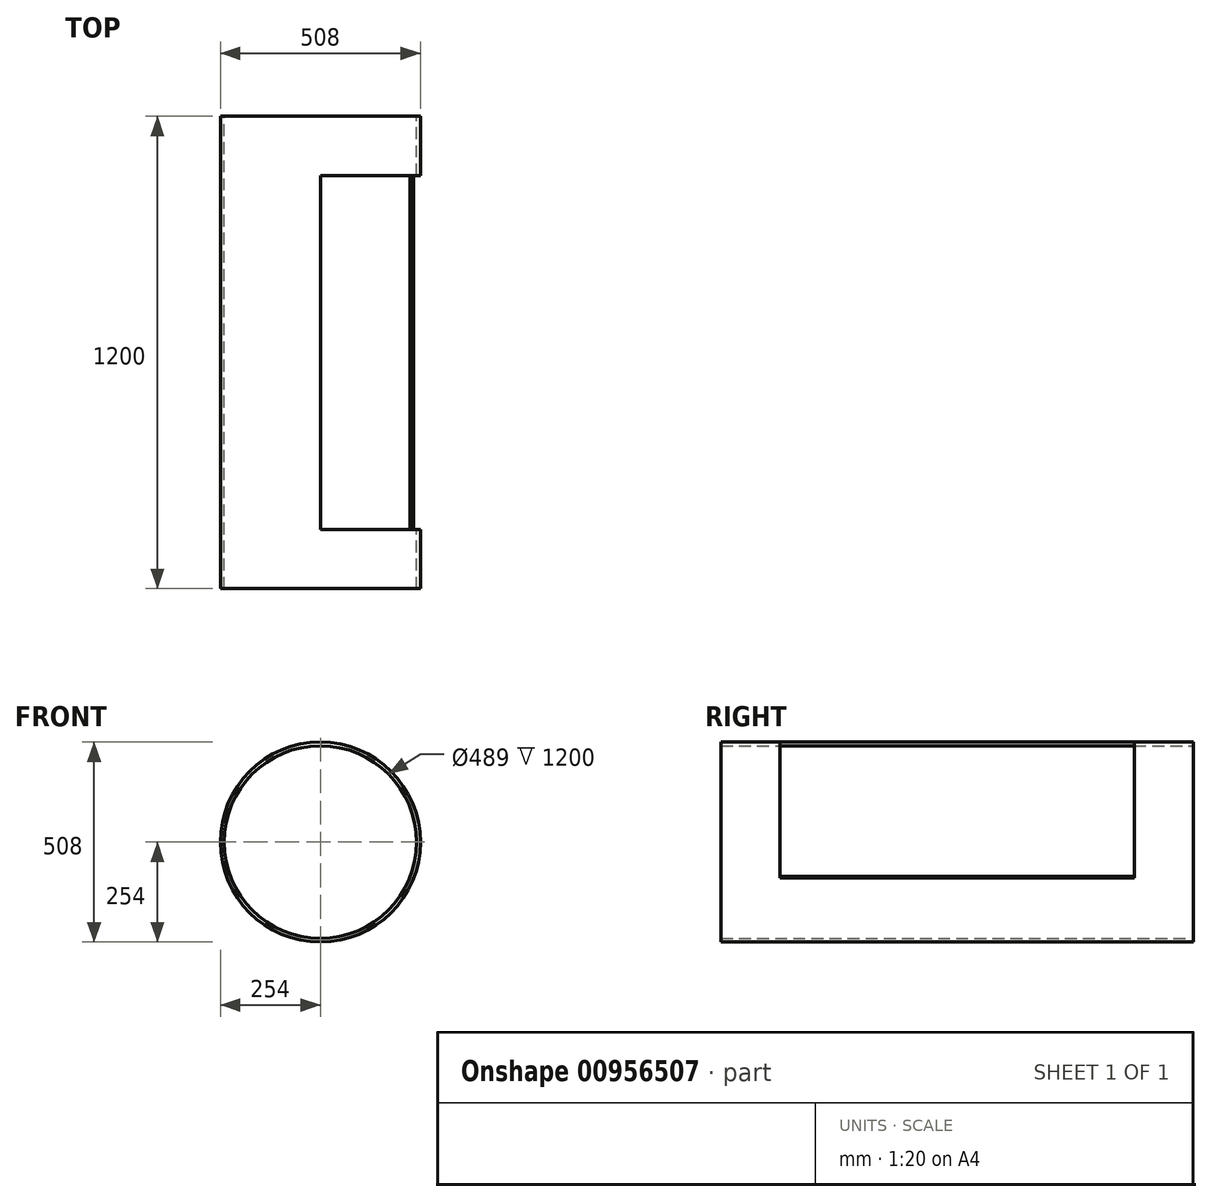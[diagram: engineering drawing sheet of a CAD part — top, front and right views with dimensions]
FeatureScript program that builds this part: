
annotation { "Feature Type Name" : "Feature", "Feature Type Description" : "" }
export const myFeature = defineFeature(function(context is Context, id is Id, definition is map)
    precondition{}
    {
        {
            var Q0;
            Q0=qCreatedBy(makeId("Front.planeOp"),FACE);
            var sketch = newSketch(context, id + "F0", { "sketchPlane" : qUnion([Q0])});
            skCircle(sketch, "E0", {"center": v(0, 0) * mm, "radius": 254 * mm});
            skCircle(sketch, "E1", {"center": v(0, 0) * mm, "radius": 244.5 * mm});
            skSolve(sketch);
        }
        {
            var Q0;
            Q0=makeQuery(id+"F0.imprint","IMPRINT",FACE,{"disambiguationData":[TD([[makeQuery(id+"F0.imprint","IMPRINT",EDGE,{"derivedFrom":sQuery(id+"F0.wireOp",EDGE,"E0")}),1.0]])]});
            extrude(context, id + "F1", {"entities" : qUnion([Q0]), "depth" : 1200 * mm, "offsetDistance" : 25.4 * mm, "symmetric" : true});
        }
        {
            var Q0;
            Q0=qCreatedBy(makeId("Front.planeOp"),FACE);
            var sketch = newSketch(context, id + "F2", { "sketchPlane" : qUnion([Q0])});
            skArc(sketch, "E2", {"start": v(0, 254) * mm, "mid": v(209.33, 143.87) * mm, "end": v(237.13, -91.03) * mm});
            skLineSegment(sketch, "E3", {"start": v(0, 254) * mm, "end": v(0, 0) * mm});
            skLineSegment(sketch, "E4", {"start": v(0, 0) * mm, "end": v(237.13, -91.03) * mm});
            skArc(sketch, "E5", {"start": v(0, 244.5) * mm, "mid": v(201.5, 138.49) * mm, "end": v(228.26, -87.62) * mm});
            skLineSegment(sketch, "E6", {"start": v(228.26, -87.62) * mm, "end": v(237.13, -91.03) * mm});
            skLineSegment(sketch, "E7", {"start": v(0, 254) * mm, "end": v(0, 244.5) * mm});
            skSolve(sketch);
        }
        {
            var Q0;
            Q0=qSketchRegion(id+"F2",true);
            extrude(context, id + "F3", {"entities" : qUnion([Q0]), "operationType" : NewBodyOperationType.REMOVE, "oppositeDirection" : true, "depth" : 900 * mm, "offsetDistance" : 25.4 * mm, "symmetric" : true});
        }
    });
